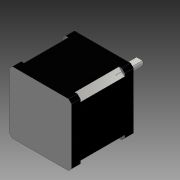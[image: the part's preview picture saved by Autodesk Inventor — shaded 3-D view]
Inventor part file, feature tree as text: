
AUTODESK INVENTOR PART (.ipt)
format: ipt  version: 2016 (Build 200138000, 138)  size: 192,000 bytes
history: native  units: mm
features: sketch x7, extrude x6, thread x4, plane x3, mirror x2, hole x1, chamfer x1, fillet x1, projected_geometry x1
ambient origin geometry x8: Origin, YZ Plane, XZ Plane, XY Plane, X Axis, Y Axis, Z Axis, Center Point
bodies: 实体1 (feature_tree)
feature tree (26):
  extrude  "拉伸1"  Depth=42.0mm TaperAngle=0.0deg
  extrude  "拉伸2"  Depth=25.0mm
  hole  "孔1"  [1 undecoded]
  thread  "螺纹1"  [1 undecoded]
  thread  "螺纹2"  [1 undecoded]
  thread  "螺纹3"  [1 undecoded]
  thread  "螺纹4"  [1 undecoded]
  plane  "工作平面2"
  extrude  "拉伸3"  Depth=10.0mm TaperAngle=0.0deg
  plane  "工作平面3"
  extrude  "拉伸4"  Depth=25.0mm TaperAngle=0.0deg
  plane  "工作平面1"
  extrude  "拉伸5"  Depth=15.0mm TaperAngle=0.0deg
  mirror  "镜像1"
  mirror  "镜像2"
  chamfer  "倒角1"  [1 undecoded]
  extrude  "拉伸6"  TaperAngle=45.0deg  [1 undecoded]
  fillet  "圆角2"  Radius=30.0mm
  sketch  "草图1"  dims[d0=42.0mm d1=42.0mm d2=0.0mm]
  sketch  "草图2"  dims[d3=30.0mm d4=25.0mm]
  sketch  "草图3"  dims[d5=1.0mm d6=0.0mm d8=3.0mm d9=18.0mm d10=18.0mm]
  sketch  "草图4"  dims[d11=3.0mm d12=0.599mm d13=4.0mm d14=2.0mm d15=90.0deg d16=10.0mm d17=20.594885mm d18=10.0mm d19=0.0mm d20=10.0mm d21=0.0mm]
  sketch  "草图5"  dims[d22=10.0mm d23=0.0mm d24=10.0mm d25=0.0mm]
  sketch  "草图6"  dims[d26=5.0mm d27=25.0mm d28=0.0mm]
  sketch  "草图7"  dims[d29=1.5mm d30=15.0mm d31=0.0mm d32=-21.0mm d34=45.0deg d35=30.0mm d36=0.0mm d37=2.0mm d38=2.0mm d39=45.0deg d40=1.0mm d41=0.0mm d42=0.5mm]
  projected_geometry  "投影回路1"
note: 7 required parameter values undecoded (feature->parameter linkage not recoverable at this tier; creation-order binding heuristic only, values carry confidence <= 0.55)
